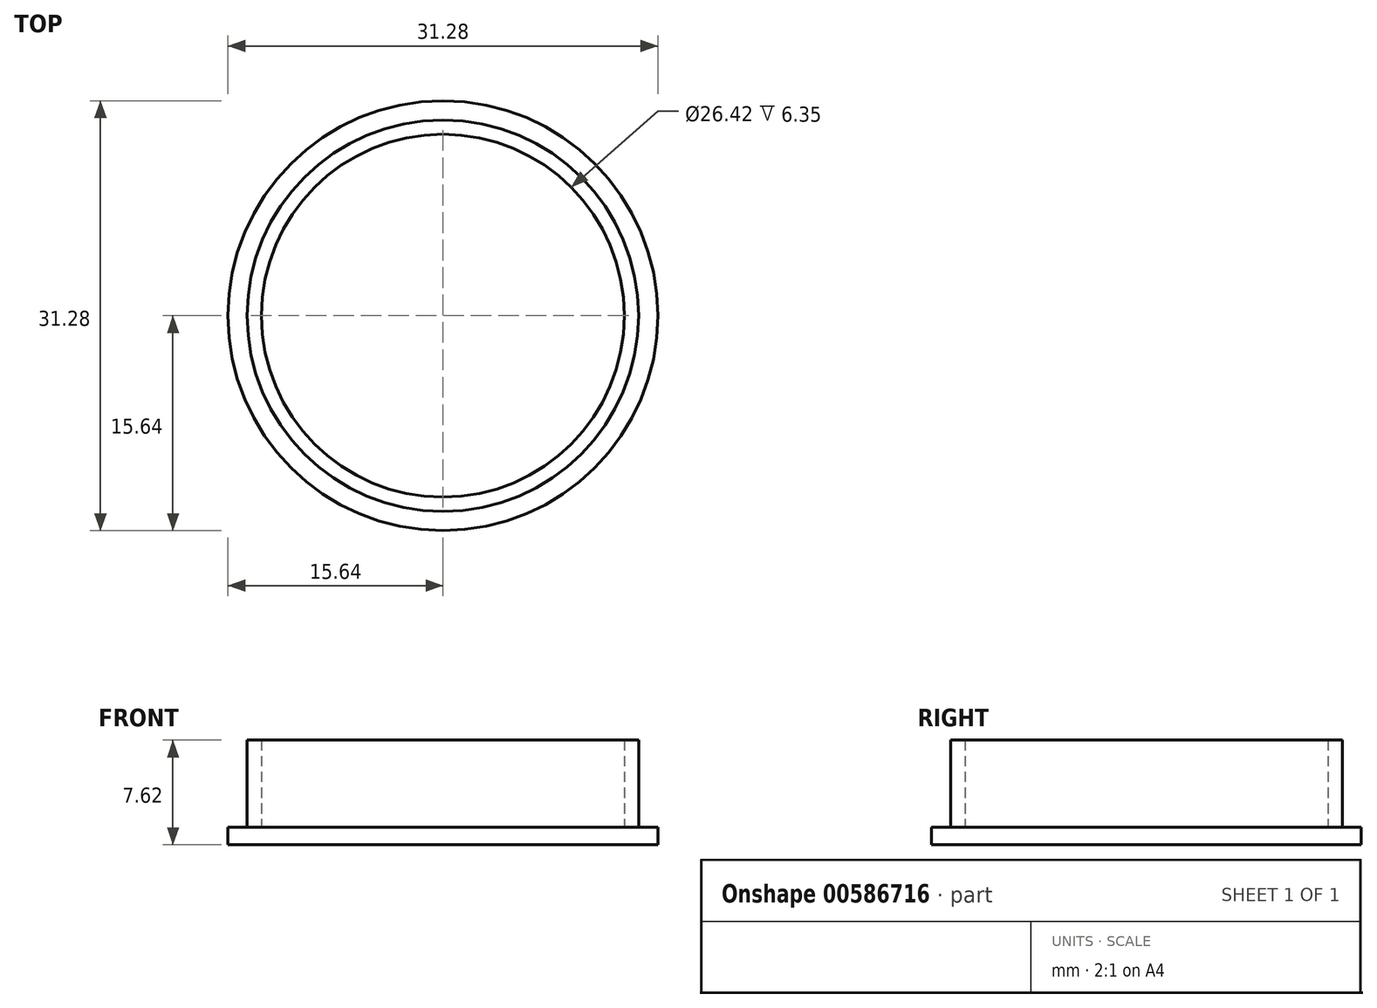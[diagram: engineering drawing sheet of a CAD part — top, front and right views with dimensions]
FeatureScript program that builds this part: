
annotation { "Feature Type Name" : "Feature", "Feature Type Description" : "" }
export const myFeature = defineFeature(function(context is Context, id is Id, definition is map)
    precondition{}
    {
        {
            var Q0;
            Q0=qCreatedBy(makeId("Top.planeOp"),FACE);
            var sketch = newSketch(context, id + "F0", { "sketchPlane" : qUnion([Q0])});
            skCircle(sketch, "E0", {"center": v(0, 0) * mm, "radius": 15.64 * mm});
            skSolve(sketch);
        }
        {
            var Q0;
            Q0=makeQuery(id+"F0.imprint","IMPRINT",FACE,{"disambiguationData":[TD([[makeQuery(id+"F0.imprint","IMPRINT",EDGE,{"derivedFrom":sQuery(id+"F0.wireOp",EDGE,"E0")}),1.0]])]});
            extrude(context, id + "F1", {"entities" : qUnion([Q0]), "depth" : 1.27 * mm, "offsetDistance" : 25.4 * mm});
        }
        {
            var Q0;
            Q0=makeQuery(id+"F1.opExtrude","CAP_FACE",FACE,{"disambiguationData":[OSD([sQuery(id+"F0.wireOp",EDGE,"E0")])],"isStart":false});
            var sketch = newSketch(context, id + "F2", { "sketchPlane" : qUnion([Q0])});
            skCircle(sketch, "E1", {"center": v(0, 0) * mm, "radius": 13.2 * mm});
            skCircle(sketch, "E2", {"center": v(0, 0) * mm, "radius": 14.25 * mm});
            skCircle(sketch, "E3", {"center": v(0, 0) * mm, "radius": 11.17 * mm});
            skSolve(sketch);
        }
        {
            var Q0;
            Q0=makeQuery(id+"F2.imprint","IMPRINT",FACE,{"disambiguationData":[TD([[makeQuery(id+"F2.imprint","IMPRINT",EDGE,{"derivedFrom":sQuery(id+"F2.wireOp",EDGE,"E1")}),-1.0]])]});
            extrude(context, id + "F3", {"entities" : qUnion([Q0]), "operationType" : NewBodyOperationType.ADD, "depth" : 6.35 * mm, "offsetDistance" : 25.4 * mm});
        }
    });
